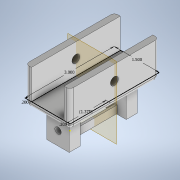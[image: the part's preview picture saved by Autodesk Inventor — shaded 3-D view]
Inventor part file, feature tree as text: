
AUTODESK INVENTOR PART (.ipt)
format: ipt  version: 2020 (Build 240168000, 168)  size: 673,280 bytes
history: native  units: in
note: dims shown in document units (in); Inventor stores cm internally (conversion verified against a paired STEP export)
features: sketch x8, extrude x5, hole x4, fillet x1, plane x1, mirror x1
ambient origin geometry x8: Origin, YZ Plane, XZ Plane, XY Plane, X Axis, Y Axis, Z Axis, Center Point
bodies: Solid1 (feature_tree)
feature tree (20):
  sketch  "Sketch1"  dims[d0=1.5in d1=3.0in]
  extrude  "Extrusion1"  Depth=3.0in
  extrude  "Extrusion2"  Depth=0.2in
  hole  "Hole1"  [1 undecoded]
  extrude  "Extrusion3"  Depth=1.0in
  hole  "Hole2"  [1 undecoded]
  fillet  "Fillet1"  Radius=0.125in
  extrude  "Extrusion4"  Depth=1.0in TaperAngle=0.0deg
  extrude  "Extrusion5"  Depth=0.125in
  hole  "Hole3"  [1 undecoded]
  hole  "Hole4"  [1 undecoded]
  sketch  "Sketch9"  dims[d23=0.45in d24=0.0787in d25=0.75in d26=0.438in d27=0.25in d28=0.5635in d29=1.0in d30=0.8108in d31=0.125in d32=0.125in d33=0.125in d34=0.5in d35=0.5in d36=90.0deg d37=0.1in d38=0.1in d39=0.125in d40=0.075in d41=0.25in d42=1.6in d43=0.0in d44=0.05in d45=0.0in d46=0.5in d47=0.5in d48=0.5in d49=0.375in d50=0.375in d51=0.375in d52=0.213in d53=0.75in d54=0.119in d55=0.25in d56=0.5635in d57=0.25in d58=0.0in d59=0.176in d60=0.75in d61=0.119in d62=0.25in d63=0.5635in d64=0.04in d65=0.0in d66=1.375in]
  plane  "Work Plane1"
  mirror  "Mirror1"
  sketch  "Sketch2"  dims[d2=0.2in d3=0.2in]
  sketch  "Sketch3"  dims[d4=1.0in d5=0.0in d6=0.2in d7=0.0in]
  sketch  "Sketch5"  dims[d8=0.5in]
  sketch  "Sketch6"  dims[d9=0.266in d10=0.75in d11=0.438in d12=0.25in d13=0.5635in d14=1.0in d15=0.8108in d16=0.5in]
  sketch  "Sketch7"  dims[d17=1.0in d18=0.75in d19=0.125in]
  sketch  "Sketch8"  dims[d20=0.125in d21=1.0in d22=0.0in]
note: 4 required parameter values undecoded (feature->parameter linkage not recoverable at this tier; creation-order binding heuristic only, values carry confidence <= 0.55)
